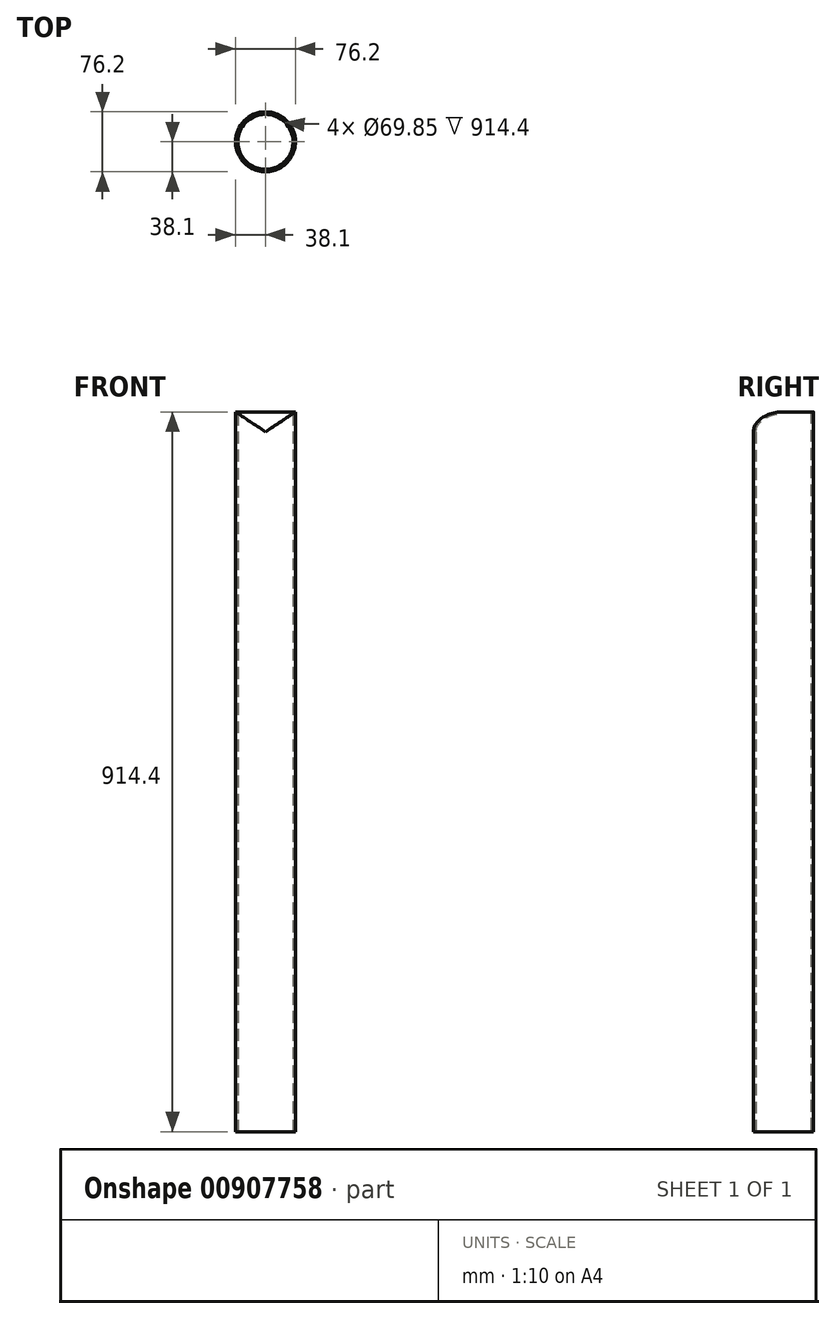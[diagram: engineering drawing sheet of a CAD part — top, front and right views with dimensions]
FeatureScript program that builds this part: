
annotation { "Feature Type Name" : "Feature", "Feature Type Description" : "" }
export const myFeature = defineFeature(function(context is Context, id is Id, definition is map)
    precondition{}
    {
        {
            var Q0;
            Q0=qCreatedBy(makeId("Top.planeOp"),FACE);
            var sketch = newSketch(context, id + "F0", { "sketchPlane" : qUnion([Q0])});
            skCircle(sketch, "E0", {"center": v(0, 0) * mm, "radius": 34.93 * mm});
            skCircle(sketch, "E1", {"center": v(0, 0) * mm, "radius": 38.1 * mm});
            skSolve(sketch);
        }
        {
            var Q0;
            Q0=makeQuery(id+"F0.imprint","IMPRINT",FACE,{"disambiguationData":[TD([[makeQuery(id+"F0.imprint","IMPRINT",EDGE,{"derivedFrom":sQuery(id+"F0.wireOp",EDGE,"E0")}),-1.0]])]});
            extrude(context, id + "F1", {"entities" : qUnion([Q0]), "depth" : 914.4 * mm, "offsetDistance" : 25.4 * mm});
        }
        {
            var Q0;
            Q0=qCreatedBy(makeId("Front.planeOp"),FACE);
            var sketch = newSketch(context, id + "F2", { "sketchPlane" : qUnion([Q0])});
            skLineSegment(sketch, "E2", {"start": v(-38.1, 914.4) * mm, "end": v(0, 889) * mm});
            skLineSegment(sketch, "E3", {"start": v(0, 889) * mm, "end": v(38.1, 914.4) * mm});
            skLineSegment(sketch, "E4", {"start": v(38.1, 914.4) * mm, "end": v(-38.1, 914.4) * mm});
            skSolve(sketch);
        }
        {
            var Q0;
            Q0=makeQuery(id+"F2.imprint","IMPRINT",FACE,{"disambiguationData":[TD([[makeQuery(id+"F2.imprint","IMPRINT",EDGE,{"derivedFrom":sQuery(id+"F2.wireOp",EDGE,"E2")}),1.0]])]});
            extrude(context, id + "F3", {"entities" : qUnion([Q0]), "operationType" : NewBodyOperationType.REMOVE, "endBound" : BoundingType.THROUGH_ALL, "depth" : 25.4 * mm, "offsetDistance" : 25.4 * mm});
        }
    });
